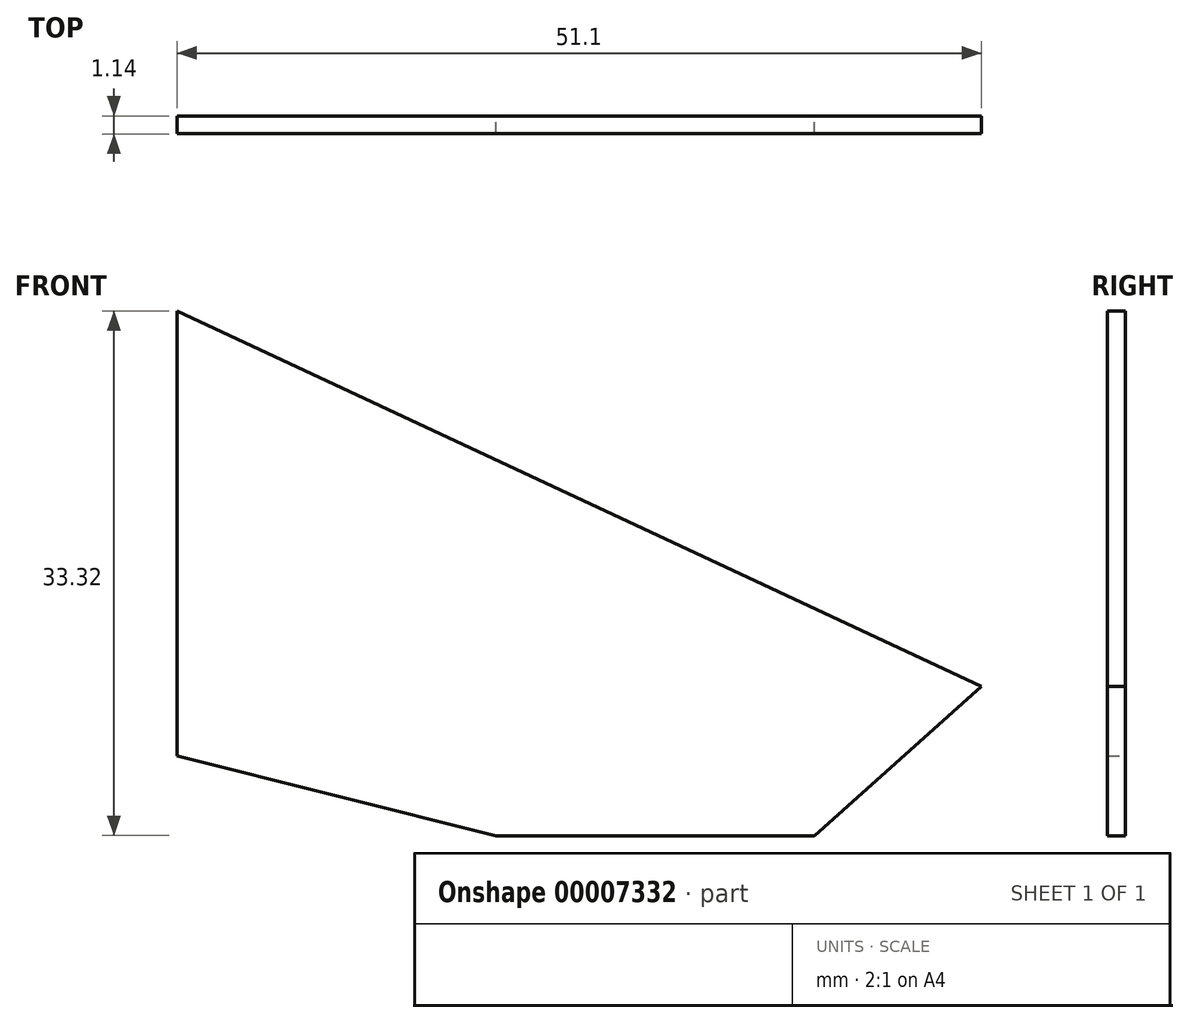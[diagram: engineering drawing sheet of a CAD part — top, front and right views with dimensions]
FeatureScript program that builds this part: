
annotation { "Feature Type Name" : "Feature", "Feature Type Description" : "" }
export const myFeature = defineFeature(function(context is Context, id is Id, definition is map)
    precondition{}
    {
        {
            var Q0;
            Q0=qCreatedBy(makeId("Front.planeOp"),FACE);
            var sketch = newSketch(context, id + "F0", { "sketchPlane" : qUnion([Q0])});
            skLineSegment(sketch, "E0", {"start": v(0, 0) * mm, "end": v(0, 28.27) * mm});
            skLineSegment(sketch, "E1", {"start": v(0, 28.27) * mm, "end": v(51.1, 4.42) * mm});
            skLineSegment(sketch, "E2", {"start": v(0, 0) * mm, "end": v(20.28, -5.05) * mm});
            skLineSegment(sketch, "E3", {"start": v(20.28, -5.05) * mm, "end": v(36.07, -9) * mm, "construction": true});
            skLineSegment(sketch, "E4", {"start": v(36.07, -9) * mm, "end": v(40.48, -5.05) * mm, "construction": true});
            skLineSegment(sketch, "E5", {"start": v(40.48, -5.05) * mm, "end": v(51.1, 4.42) * mm});
            skLineSegment(sketch, "E6", {"start": v(20.28, -5.05) * mm, "end": v(40.48, -5.05) * mm});
            skSolve(sketch);
        }
        {
            var Q0;
            Q0 = qSketchRegion(id + "F0", true);
            extrude(context, id + "F1", {"entities" : qUnion([Q0]), "depth" : 0.57 * mm});
        }
        {
            var Q0;
            Q0 = qSketchRegion(id + "F0", true);
            extrude(context, id + "F2", {"entities" : qUnion([Q0]), "operationType" : NewBodyOperationType.ADD, "oppositeDirection" : true, "depth" : 0.57 * mm});
        }
    });
